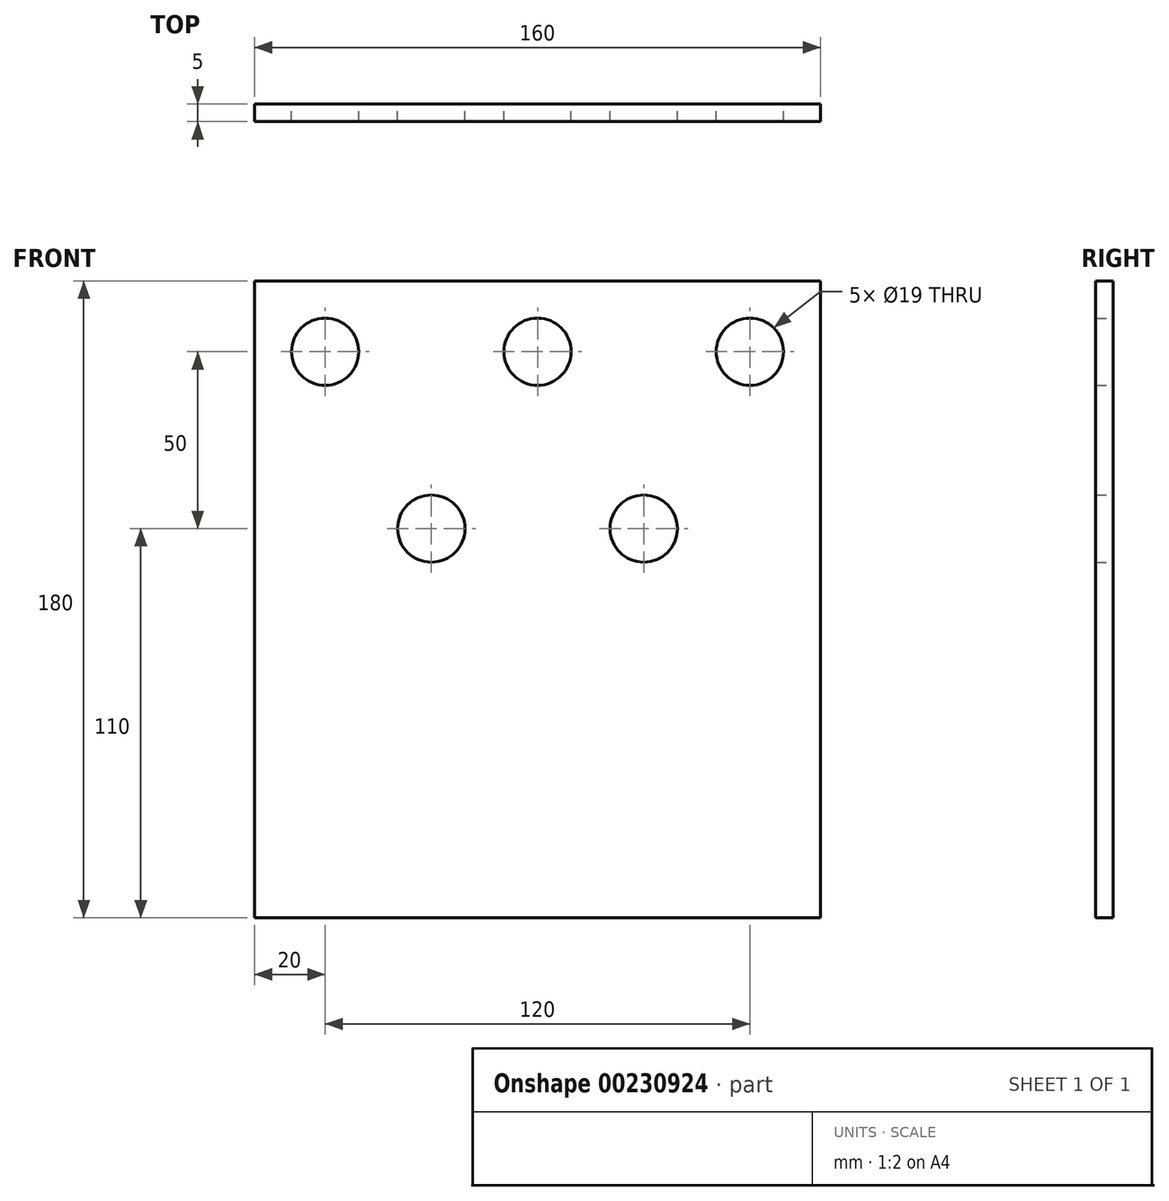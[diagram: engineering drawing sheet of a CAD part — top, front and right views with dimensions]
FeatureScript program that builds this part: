
annotation { "Feature Type Name" : "Feature", "Feature Type Description" : "" }
export const myFeature = defineFeature(function(context is Context, id is Id, definition is map)
    precondition{}
    {
        {
            var Q0;
            Q0=qCreatedBy(makeId("Front.planeOp"),FACE);
            var sketch = newSketch(context, id + "F0", { "sketchPlane" : qUnion([Q0])});
            skLineSegment(sketch, "E0.bottom", {"start": v(0, 0) * mm, "end": v(160, 0) * mm});
            skLineSegment(sketch, "E0.top", {"start": v(0, 180) * mm, "end": v(160, 180) * mm});
            skLineSegment(sketch, "E0.left", {"start": v(0, 0) * mm, "end": v(0, 180) * mm});
            skLineSegment(sketch, "E0.right", {"start": v(160, 0) * mm, "end": v(160, 180) * mm});
            skCircle(sketch, "E1", {"center": v(20, 160) * mm, "radius": 9.5 * mm});
            skCircle(sketch, "E2", {"center": v(80, 160) * mm, "radius": 9.5 * mm});
            skCircle(sketch, "E3", {"center": v(140, 160) * mm, "radius": 9.5 * mm});
            skCircle(sketch, "E4", {"center": v(50, 110) * mm, "radius": 9.5 * mm});
            skCircle(sketch, "E5", {"center": v(110, 110) * mm, "radius": 9.5 * mm});
            skSolve(sketch);
        }
        {
            var Q0;
            Q0=makeQuery(id+"F0.imprint","IMPRINT",FACE,{"disambiguationData":[TD([[makeQuery(id+"F0.imprint","IMPRINT",EDGE,{"derivedFrom":sQuery(id+"F0.wireOp",EDGE,"E0.bottom")}),1.0]])]});
            extrude(context, id + "F1", {"entities" : qUnion([Q0]), "depth" : 5 * mm});
        }
    });
